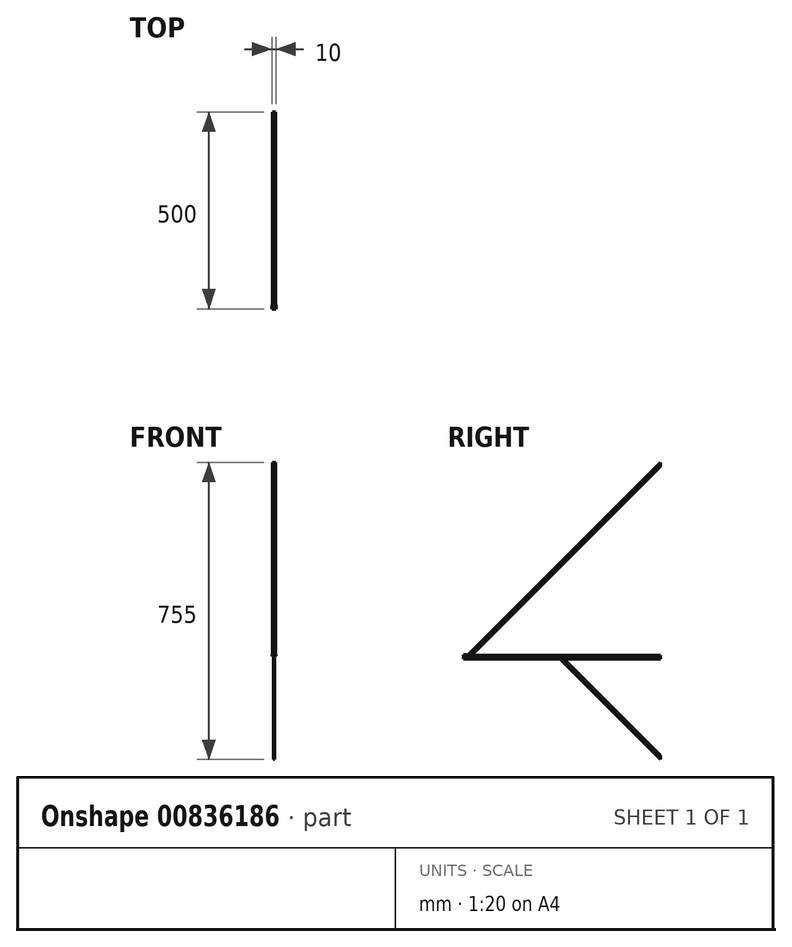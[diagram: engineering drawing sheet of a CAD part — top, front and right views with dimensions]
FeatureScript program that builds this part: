
annotation { "Feature Type Name" : "Feature", "Feature Type Description" : "" }
export const myFeature = defineFeature(function(context is Context, id is Id, definition is map)
    precondition{}
    {
        {
            var Q0;
            Q0=qCreatedBy(makeId("Front.planeOp"),FACE);
            var sketch = newSketch(context, id + "F0", { "sketchPlane" : qUnion([Q0])});
            skLineSegment(sketch, "E0.top", {"start": v(-1.25, -3.75) * mm, "end": v(1.25, -3.75) * mm});
            skLineSegment(sketch, "E0.left", {"start": v(-1.25, 3.75) * mm, "end": v(-1.25, -3.75) * mm});
            skLineSegment(sketch, "E0.right", {"start": v(1.25, 3.75) * mm, "end": v(1.25, -3.75) * mm});
            skPoint(sketch, "E0.middle", {"position": v(0, 0) * mm});
            skPoint(sketch, "E1", {"position": v(0, 5) * mm});
            skLineSegment(sketch, "E2.bottom", {"start": v(-3.75, 6.25) * mm, "end": v(3.75, 6.25) * mm});
            skLineSegment(sketch, "E2.top", {"start": v(-3.75, 3.75) * mm, "end": v(-1.25, 3.75) * mm});
            skLineSegment(sketch, "E2.left", {"start": v(-3.75, 6.25) * mm, "end": v(-3.75, 3.75) * mm});
            skLineSegment(sketch, "E2.right", {"start": v(3.75, 6.25) * mm, "end": v(3.75, 3.75) * mm});
            skLineSegment(sketch, "E3.trimOffspring", {"start": v(1.25, 3.75) * mm, "end": v(3.75, 3.75) * mm});
            skSolve(sketch);
        }
        {
            var Q0;
            Q0 = qSketchRegion(id + "F0", true);
            var Q1;
            Q1=makeQuery(id+"F0.imprint","IMPRINT",FACE,{"disambiguationData":[TD([[makeQuery(id+"F0.imprint","IMPRINT",EDGE,{"derivedFrom":sQuery(id+"F0.wireOp",EDGE,"E0.top")}),1.0]])]});
            extrude(context, id + "F1", {"entities" : qUnion([Q0, Q1]), "depth" : 500 * mm, "offsetDistance" : 25 * mm});
        }
        {
            var Q0;
            Q0=makeQuery(id+"F1.opExtrude","SWEPT_FACE",FACE,{"disambiguationData":[OSD([sQuery(id+"F0.wireOp",EDGE,"E2.left")])]});
            var sketch = newSketch(context, id + "F2", { "sketchPlane" : qUnion([Q0])});
            skPoint(sketch, "E4", {"position": v(490, 6.25) * mm});
            skLineSegment(sketch, "E5", {"start": v(0, 551.85) * mm, "end": v(0, -821.01) * mm});
            skPoint(sketch, "E6", {"position": v(0, 496.25) * mm});
            skPoint(sketch, "E7", {"position": v(0, 6.25) * mm});
            skPoint(sketch, "E8", {"position": v(0, 486.25) * mm});
            skPoint(sketch, "E9", {"position": v(480, 6.25) * mm});
            skLineSegment(sketch, "E10", {"start": v(0, 486.25) * mm, "end": v(480, 6.25) * mm});
            skLineSegment(sketch, "E11", {"start": v(0, 496.25) * mm, "end": v(490, 6.25) * mm});
            skSolve(sketch);
        }
        {
            var Q0;
            {var subQ0=sQuery(id+"F2.wireOp",EDGE,"E10");Q0=makeQuery(id+"F2.imprint","IMPRINT",FACE,{"disambiguationData":[TD([[makeQuery(id+"F2.imprint","IMPRINT",EDGE,{"derivedFrom":subQ0}),1.0]])]});}
            extrude(context, id + "F3", {"entities" : qUnion([Q0]), "depth" : -7.5 * mm, "offsetDistance" : 25 * mm});
        }
        {
            var Q0;
            Q0=makeQuery(id+"F1.opExtrude","SWEPT_FACE",FACE,{"disambiguationData":[OSD([sQuery(id+"F0.wireOp",EDGE,"E0.left")])]});
            var sketch = newSketch(context, id + "F4", { "sketchPlane" : qUnion([Q0])});
            skPoint(sketch, "E12", {"position": v(250, -3.75) * mm});
            skPoint(sketch, "E13", {"position": v(245, -3.75) * mm});
            skPoint(sketch, "E14", {"position": v(255, -3.75) * mm});
            skLineSegment(sketch, "E15", {"start": v(0, 548.21) * mm, "end": v(0, -398.22) * mm});
            skPoint(sketch, "E16", {"position": v(0, -248.75) * mm});
            skPoint(sketch, "E17", {"position": v(0, -258.75) * mm});
            skLineSegment(sketch, "E18", {"start": v(0, -248.75) * mm, "end": v(245, -3.75) * mm});
            skLineSegment(sketch, "E19", {"start": v(0, -258.75) * mm, "end": v(255, -3.75) * mm});
            skSolve(sketch);
        }
        {
            var Q0;
            {var subQ0=sQuery(id+"F4.wireOp",EDGE,"E18");Q0=makeQuery(id+"F4.imprint","IMPRINT",FACE,{"disambiguationData":[TD([[makeQuery(id+"F4.imprint","IMPRINT",EDGE,{"derivedFrom":subQ0}),-1.0]])]});}
            extrude(context, id + "F5", {"entities" : qUnion([Q0]), "depth" : -2.5 * mm, "offsetDistance" : 25 * mm});
        }
        {
            var Q0;
            Q0=makeQuery(id+"F1.opExtrude","SWEPT_FACE",FACE,{"disambiguationData":[OSD([sQuery(id+"F0.wireOp",EDGE,"E2.bottom")])]});
            var sketch = newSketch(context, id + "F6", { "sketchPlane" : qUnion([Q0])});
            skPoint(sketch, "E20", {"position": v(0, -495) * mm});
            skLineSegment(sketch, "E21.bottom", {"start": v(-5, -490) * mm, "end": v(5, -490) * mm});
            skLineSegment(sketch, "E21.top", {"start": v(-5, -500) * mm, "end": v(5, -500) * mm});
            skLineSegment(sketch, "E21.left", {"start": v(-5, -490) * mm, "end": v(-5, -500) * mm});
            skLineSegment(sketch, "E21.right", {"start": v(5, -490) * mm, "end": v(5, -500) * mm});
            skSolve(sketch);
        }
        {
            var Q0;
            {var subQ0=sQuery(id+"F6.wireOp",EDGE,"E21.right");Q0=makeQuery(id+"F6.imprint","IMPRINT",FACE,{"disambiguationData":[TD([[makeQuery(id+"F6.imprint","IMPRINT",EDGE,{"derivedFrom":subQ0}),-1.0]])]});}
            var Q1;
            {var subQ0=sQuery(id+"F6.wireOp",EDGE,"E21.bottom");var subQ1=sQuery(id+"F0.wireOp",EDGE,"E2.bottom");var subQ2=makeQuery(id+"F1.opExtrude","SWEPT_EDGE",EDGE,{"disambiguationData":[OSD([subQ1,sQuery(id+"F0.wireOp",EDGE,"E2.left")])]});var subQ3=makeQuery(id+"F6.imprint","INTERSECT",VERTEX,{"derivedFrom":[subQ2,subQ0]});Q1=makeQuery(id+"F6.imprint","IMPRINT",FACE,{"disambiguationData":[TD([[makeQuery(id+"F6.imprint","IMPRINT",EDGE,{"disambiguationData":[TD([[subQ3,-1.0]])],"derivedFrom":subQ0}),-1.0]])]});}
            var Q2;
            {var subQ0=sQuery(id+"F6.wireOp",EDGE,"E21.left");Q2=makeQuery(id+"F6.imprint","IMPRINT",FACE,{"disambiguationData":[TD([[makeQuery(id+"F6.imprint","IMPRINT",EDGE,{"derivedFrom":subQ0}),1.0]])]});}
            extrude(context, id + "F7", {"entities" : qUnion([Q0, Q1, Q2]), "operationType" : NewBodyOperationType.ADD, "depth" : 0.5 * mm, "offsetDistance" : 25 * mm});
        }
    });
